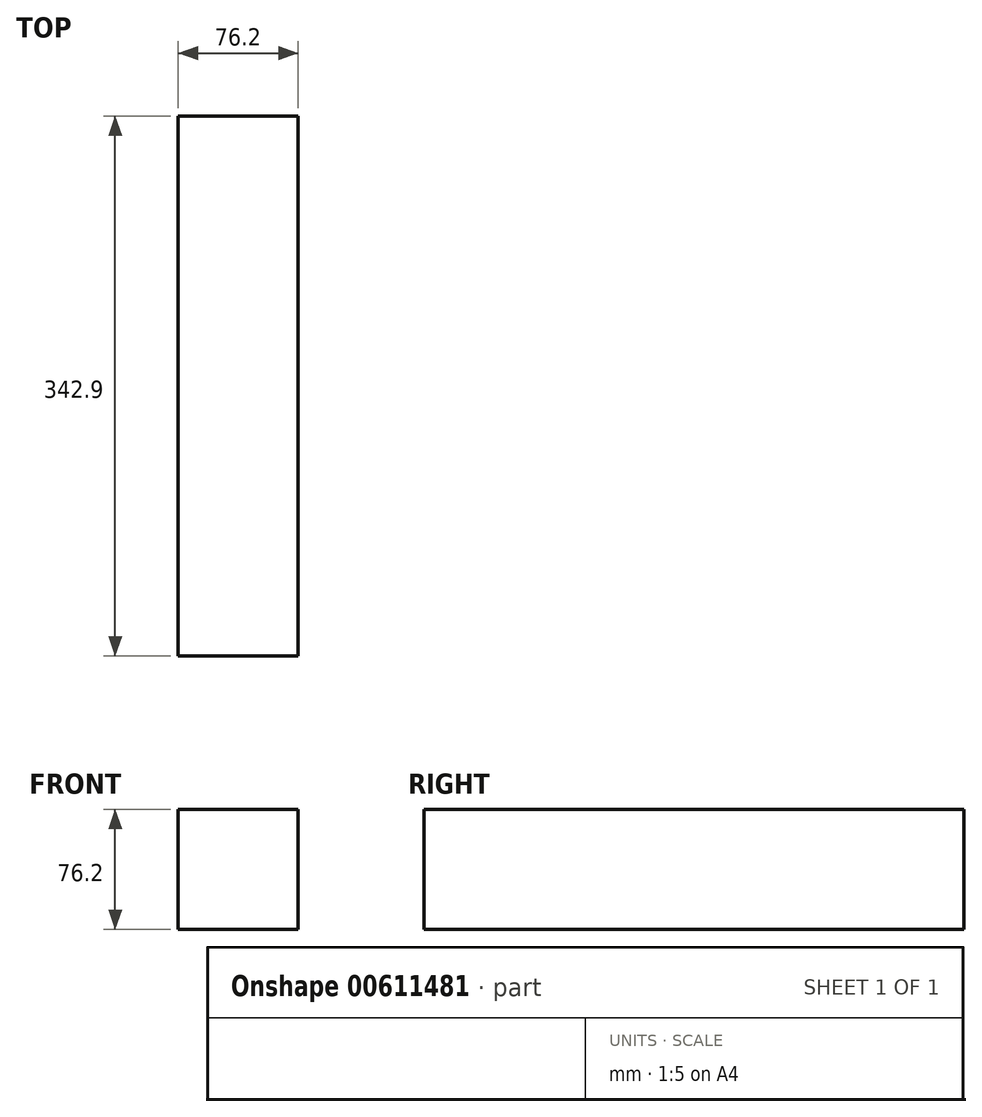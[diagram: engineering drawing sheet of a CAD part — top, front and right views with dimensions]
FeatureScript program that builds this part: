
annotation { "Feature Type Name" : "Feature", "Feature Type Description" : "" }
export const myFeature = defineFeature(function(context is Context, id is Id, definition is map)
    precondition{}
    {
        {
            var Q0;
            Q0=qCreatedBy(makeId("Front.planeOp"),FACE);
            var sketch = newSketch(context, id + "F0", { "sketchPlane" : qUnion([Q0])});
            skLineSegment(sketch, "E0.bottom", {"start": v(0, 0) * mm, "end": v(76.2, 0) * mm});
            skLineSegment(sketch, "E0.top", {"start": v(0, -76.2) * mm, "end": v(76.2, -76.2) * mm});
            skLineSegment(sketch, "E0.left", {"start": v(0, 0) * mm, "end": v(0, -76.2) * mm});
            skLineSegment(sketch, "E0.right", {"start": v(76.2, 0) * mm, "end": v(76.2, -76.2) * mm});
            skSolve(sketch);
        }
        {
            var Q0;
            Q0 = qSketchRegion(id + "F0", true);
            extrude(context, id + "F1", {"entities" : qUnion([Q0]), "depth" : 342.9 * mm, "offsetDistance" : 25.4 * mm});
        }
    });
